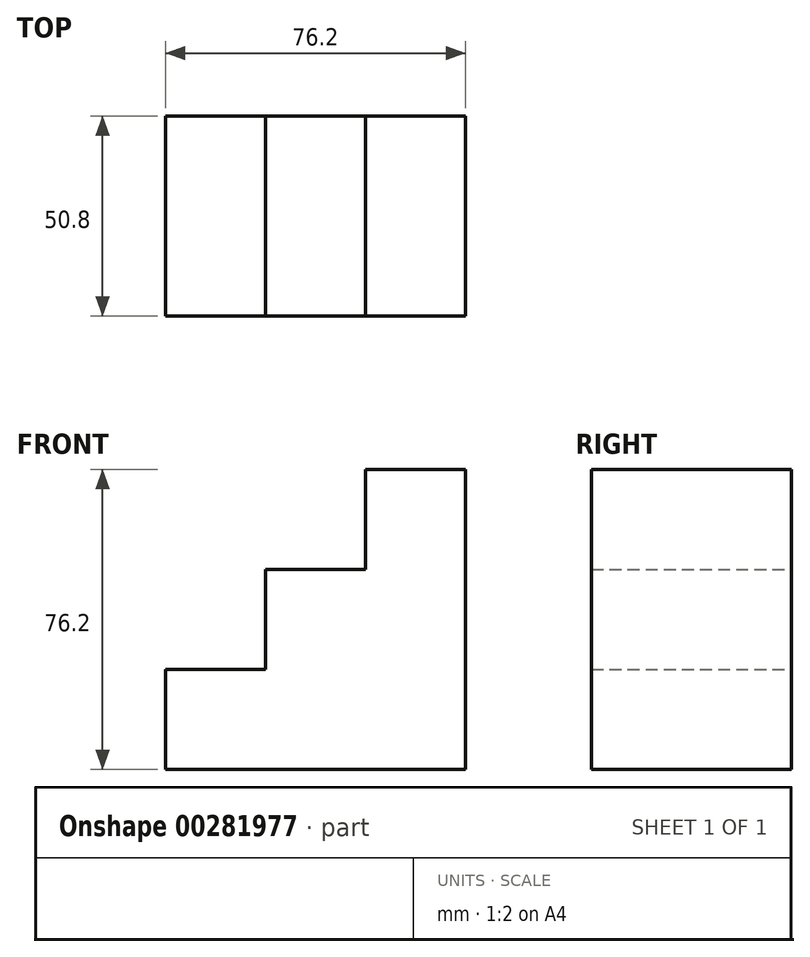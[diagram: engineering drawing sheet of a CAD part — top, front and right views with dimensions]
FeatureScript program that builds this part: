
annotation { "Feature Type Name" : "Feature", "Feature Type Description" : "" }
export const myFeature = defineFeature(function(context is Context, id is Id, definition is map)
    precondition{}
    {
        {
            var Q0;
            Q0=qCreatedBy(makeId("Front.planeOp"),FACE);
            var sketch = newSketch(context, id + "F0", { "sketchPlane" : qUnion([Q0])});
            skLineSegment(sketch, "E0", {"start": v(0, 0) * mm, "end": v(0, 76.2) * mm});
            skLineSegment(sketch, "E1", {"start": v(-25.4, 76.2) * mm, "end": v(0, 76.2) * mm});
            skLineSegment(sketch, "E2", {"start": v(-25.4, 76.2) * mm, "end": v(-25.4, 50.8) * mm});
            skLineSegment(sketch, "E3", {"start": v(-50.8, 50.8) * mm, "end": v(-25.4, 50.8) * mm});
            skLineSegment(sketch, "E4", {"start": v(-50.8, 25.4) * mm, "end": v(-50.8, 50.8) * mm});
            skLineSegment(sketch, "E5", {"start": v(-50.8, 25.4) * mm, "end": v(-76.2, 25.4) * mm});
            skLineSegment(sketch, "E6", {"start": v(-76.2, 0) * mm, "end": v(-76.2, 25.4) * mm});
            skLineSegment(sketch, "E7", {"start": v(-76.2, 0) * mm, "end": v(0, 0) * mm});
            skSolve(sketch);
        }
        {
            var Q0;
            Q0 = qSketchRegion(id + "F0", true);
            extrude(context, id + "F1", {"entities" : qUnion([Q0]), "depth" : 50.8 * mm});
        }
    });
